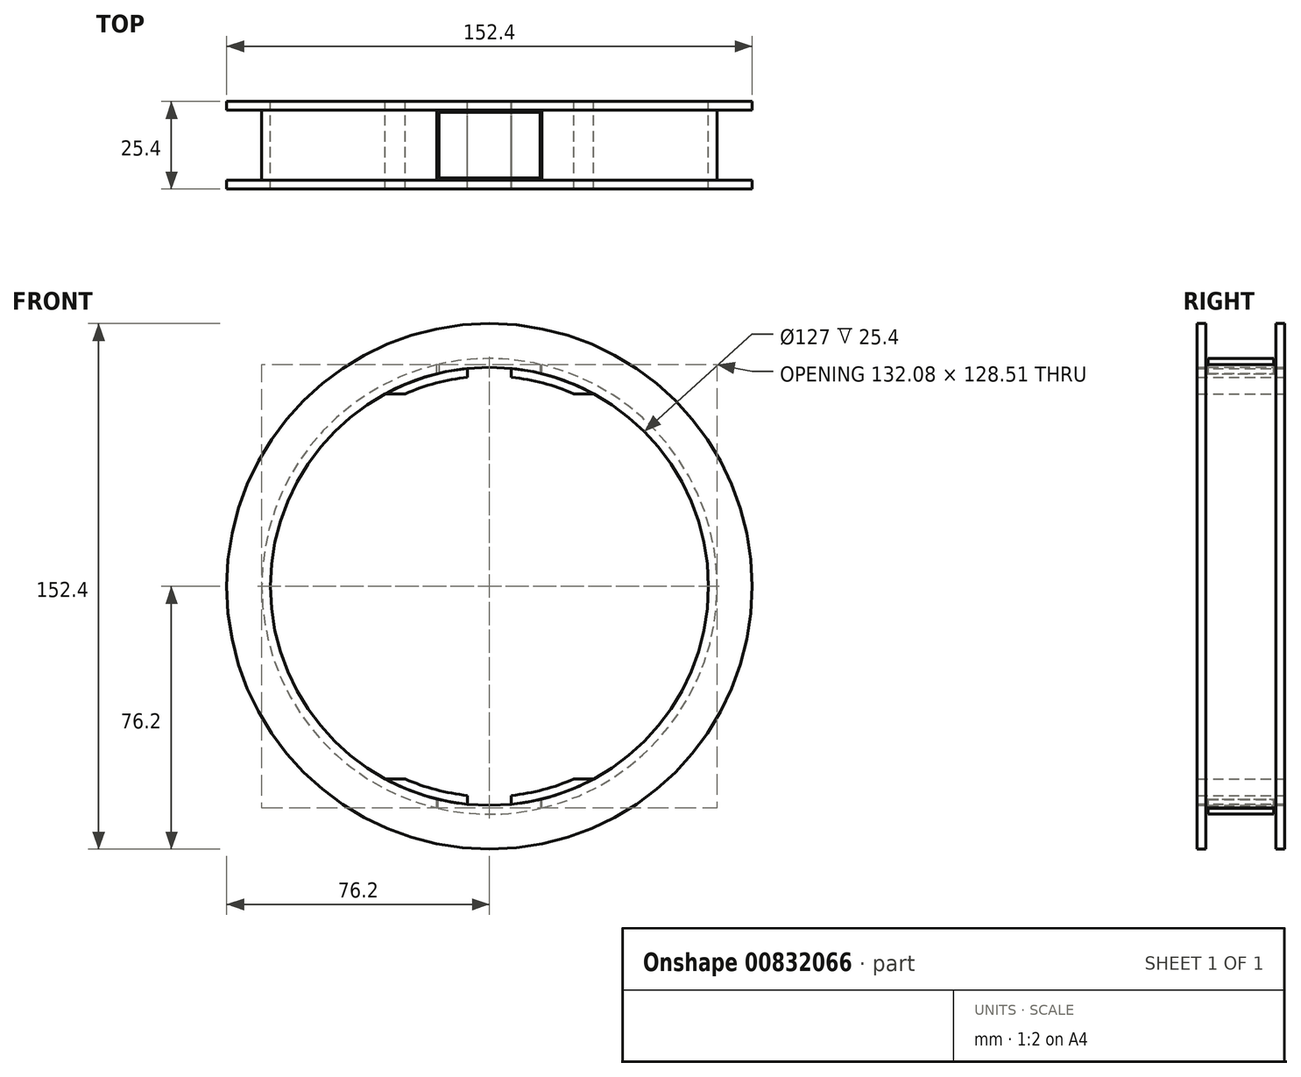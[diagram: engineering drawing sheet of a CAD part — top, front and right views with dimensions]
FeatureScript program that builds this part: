
annotation { "Feature Type Name" : "Feature", "Feature Type Description" : "" }
export const myFeature = defineFeature(function(context is Context, id is Id, definition is map)
    precondition{}
    {
        {
            var Q0;
            Q0=qCreatedBy(makeId("Front.planeOp"),FACE);
            var sketch = newSketch(context, id + "F0", { "sketchPlane" : qUnion([Q0])});
            skCircle(sketch, "E0", {"center": v(0, 0) * mm, "radius": 63.5 * mm});
            skCircle(sketch, "E1", {"center": v(0, 0) * mm, "radius": 76.2 * mm});
            skSolve(sketch);
        }
        {
            var Q0;
            Q0=qSketchRegion(id+"F0",true);
            extrude(context, id + "F1", {"entities" : qUnion([Q0]), "depth" : 25.4 * mm, "offsetDistance" : 25.4 * mm, "symmetric" : true});
        }
        {
            var Q0;
            Q0=qCreatedBy(makeId("Top.planeOp"),FACE);
            var sketch = newSketch(context, id + "F2", { "sketchPlane" : qUnion([Q0])});
            skLineSegment(sketch, "E2", {"start": v(-15.24, -10.16) * mm, "end": v(-15.24, 10.16) * mm});
            skLineSegment(sketch, "E3", {"start": v(15.24, -10.16) * mm, "end": v(15.24, 10.16) * mm});
            skLineSegment(sketch, "E4", {"start": v(15.24, -10.16) * mm, "end": v(-15.24, -10.16) * mm});
            skLineSegment(sketch, "E5", {"start": v(15.24, 10.16) * mm, "end": v(-15.24, 10.16) * mm});
            skLineSegment(sketch, "E6", {"start": v(0, 39.62) * mm, "end": v(0, -54.89) * mm});
            skLineSegment(sketch, "E7", {"start": v(22.27, 0) * mm, "end": v(-22.66, 0) * mm, "construction": true});
            skPoint(sketch, "E7.startSnap0", {"position": v(-15.24, 0) * mm});
            skSolve(sketch);
        }
        {
            var Q0;
            Q0=makeQuery(id+"F1.opExtrude","SWEPT_FACE",FACE,{"disambiguationData":[OSD([sQuery(id+"F0.wireOp",EDGE,"E1")])]});
            shell(context, id + "F3", {"entities" : qUnion([Q0]), "thickness" : 2.54 * mm});
        }
        {
            var Q0;
            Q0=qSketchRegion(id+"F2",true);
            extrude(context, id + "F4", {"entities" : qUnion([Q0]), "operationType" : NewBodyOperationType.REMOVE, "oppositeDirection" : true, "depth" : 132.08 * mm, "offsetDistance" : 25.4 * mm, "symmetric" : true});
        }
        {
            var Q0;
            Q0=qCreatedBy(makeId("Front.planeOp"),FACE);
            var sketch = newSketch(context, id + "F5", { "sketchPlane" : qUnion([Q0])});
            skArc(sketch, "E8", {"start": v(14.74, 61.76) * mm, "mid": v(0.03, 63.5) * mm, "end": v(-14.68, 61.78) * mm});
            skArc(sketch, "E9", {"start": v(-14.96, -64.32) * mm, "mid": v(-0.07, -66.04) * mm, "end": v(14.83, -64.35) * mm});
            skLineSegment(sketch, "E10", {"start": v(-14.68, 64.39) * mm, "end": v(-14.68, 61.78) * mm});
            skLineSegment(sketch, "E11", {"start": v(14.74, 64.37) * mm, "end": v(14.74, 61.76) * mm});
            skLineSegment(sketch, "E12", {"start": v(14.83, -61.74) * mm, "end": v(14.83, -64.35) * mm});
            skLineSegment(sketch, "E13", {"start": v(-14.96, -64.32) * mm, "end": v(-14.96, -61.71) * mm});
            skArc(sketch, "E14.trimOffspring", {"start": v(-14.96, -61.71) * mm, "mid": v(-0.07, -63.5) * mm, "end": v(14.83, -61.74) * mm});
            skArc(sketch, "E15.trimOffspring", {"start": v(14.74, 64.37) * mm, "mid": v(0.03, 66.04) * mm, "end": v(-14.68, 64.39) * mm});
            skSolve(sketch);
        }
        {
            var Q0;
            Q0=qSketchRegion(id+"F5",true);
            extrude(context, id + "F6", {"entities" : qUnion([Q0]), "depth" : 19.05 * mm, "offsetDistance" : 25.4 * mm, "symmetric" : true});
        }
        {
            var Q0;
            Q0=qCreatedBy(makeId("Front.planeOp"),FACE);
            var sketch = newSketch(context, id + "F7", { "sketchPlane" : qUnion([Q0])});
            skArc(sketch, "E16", {"start": v(-24.43, -55.85) * mm, "mid": v(-15.58, -58.94) * mm, "end": v(-6.35, -60.63) * mm});
            skLineSegment(sketch, "E17", {"start": v(-6.35, 60.63) * mm, "end": v(-6.35, 63.17) * mm});
            skLineSegment(sketch, "E18", {"start": v(6.35, 63.17) * mm, "end": v(6.35, 60.63) * mm});
            skLineSegment(sketch, "E19", {"start": v(29.54, 56.4) * mm, "end": v(23.14, 56.4) * mm});
            skLineSegment(sketch, "E20.trimOffspring", {"start": v(-23.14, 56.4) * mm, "end": v(-29.35, 56.4) * mm});
            skLineSegment(sketch, "E21", {"start": v(-6.35, -63.17) * mm, "end": v(-6.35, -60.63) * mm});
            skLineSegment(sketch, "E22", {"start": v(6.35, -63.17) * mm, "end": v(6.35, -60.63) * mm});
            skLineSegment(sketch, "E23", {"start": v(-30.22, -55.85) * mm, "end": v(-24.43, -55.85) * mm});
            skArc(sketch, "E24", {"start": v(-30.22, -55.85) * mm, "mid": v(-18.62, -60.7) * mm, "end": v(-6.29, -63.19) * mm});
            skArc(sketch, "E25.trimOffspring", {"start": v(23.14, 56.4) * mm, "mid": v(14.9, 59.11) * mm, "end": v(6.35, 60.63) * mm});
            skArc(sketch, "E26.trimOffspring", {"start": v(6.35, -60.63) * mm, "mid": v(15.58, -58.94) * mm, "end": v(24.43, -55.85) * mm});
            skArc(sketch, "E27.trimOffspring", {"start": v(-6.35, 60.63) * mm, "mid": v(-14.9, 59.11) * mm, "end": v(-23.14, 56.4) * mm});
            skArc(sketch, "E28.trimOffspring", {"start": v(-6.35, 63.18) * mm, "mid": v(-18.09, 60.87) * mm, "end": v(-29.18, 56.4) * mm});
            skLineSegment(sketch, "E29", {"start": v(24.43, -55.85) * mm, "end": v(30.22, -55.85) * mm});
            skArc(sketch, "E30.trimOffspring", {"start": v(29.18, 56.4) * mm, "mid": v(18.09, 60.87) * mm, "end": v(6.35, 63.18) * mm});
            skArc(sketch, "E31.trimOffspring", {"start": v(6.4, -63.18) * mm, "mid": v(18.67, -60.7) * mm, "end": v(30.22, -55.85) * mm});
            skLineSegment(sketch, "E32.trimOffspring", {"start": v(6.35, -63.13) * mm, "end": v(6.4, -63.18) * mm});
            skLineSegment(sketch, "E33.MirrorCS", {"start": v(-6.35, -63.13) * mm, "end": v(-6.4, -63.18) * mm});
            skArc(sketch, "E34.MirrorCS", {"start": v(-6.35, -60.63) * mm, "mid": v(-15.58, -58.94) * mm, "end": v(-24.43, -55.85) * mm});
            skLineSegment(sketch, "E35.MirrorCS", {"start": v(-24.43, -55.85) * mm, "end": v(-30.22, -55.85) * mm});
            skArc(sketch, "E36.MirrorCS", {"start": v(-6.4, -63.18) * mm, "mid": v(-18.67, -60.7) * mm, "end": v(-30.22, -55.85) * mm});
            skLineSegment(sketch, "E37.MirrorCS", {"start": v(30.22, -55.85) * mm, "end": v(24.43, -55.85) * mm});
            skArc(sketch, "E38.MirrorCS", {"start": v(30.22, -55.85) * mm, "mid": v(18.62, -60.7) * mm, "end": v(6.29, -63.19) * mm});
            skArc(sketch, "E39.MirrorCS", {"start": v(24.43, -55.85) * mm, "mid": v(15.58, -58.94) * mm, "end": v(6.35, -60.63) * mm});
            skLineSegment(sketch, "E40.MirrorCS", {"start": v(6.35, 63.13) * mm, "end": v(6.4, 63.18) * mm});
            skLineSegment(sketch, "E41.MirrorCS", {"start": v(-6.35, 63.13) * mm, "end": v(-6.4, 63.18) * mm});
            skLineSegment(sketch, "E42.MirrorCS", {"start": v(-6.35, 63.17) * mm, "end": v(-6.35, 60.63) * mm});
            skLineSegment(sketch, "E43.MirrorCS", {"start": v(24.43, 55.85) * mm, "end": v(30.22, 55.85) * mm});
            skLineSegment(sketch, "E44.MirrorCS", {"start": v(-24.43, 55.85) * mm, "end": v(-30.22, 55.85) * mm});
            skArc(sketch, "E45.MirrorCS", {"start": v(6.4, 63.18) * mm, "mid": v(18.67, 60.7) * mm, "end": v(30.22, 55.85) * mm});
            skLineSegment(sketch, "E46.MirrorCS", {"start": v(-30.22, 55.85) * mm, "end": v(-24.43, 55.85) * mm});
            skArc(sketch, "E47.MirrorCS", {"start": v(-6.35, 60.63) * mm, "mid": v(-15.58, 58.94) * mm, "end": v(-24.43, 55.85) * mm});
            skArc(sketch, "E48.MirrorCS", {"start": v(-6.4, 63.18) * mm, "mid": v(-18.67, 60.7) * mm, "end": v(-30.22, 55.85) * mm});
            skArc(sketch, "E49.MirrorCS", {"start": v(6.35, 60.63) * mm, "mid": v(15.58, 58.94) * mm, "end": v(24.43, 55.85) * mm});
            skLineSegment(sketch, "E50.MirrorCS", {"start": v(30.22, 55.85) * mm, "end": v(24.43, 55.85) * mm});
            skArc(sketch, "E51.MirrorCS", {"start": v(30.22, 55.85) * mm, "mid": v(18.62, 60.7) * mm, "end": v(6.29, 63.19) * mm});
            skArc(sketch, "E52.MirrorCS", {"start": v(-24.43, 55.85) * mm, "mid": v(-15.58, 58.94) * mm, "end": v(-6.35, 60.63) * mm});
            skArc(sketch, "E53.MirrorCS", {"start": v(24.43, 55.85) * mm, "mid": v(15.58, 58.94) * mm, "end": v(6.35, 60.63) * mm});
            skArc(sketch, "E54.MirrorCS", {"start": v(-30.22, 55.85) * mm, "mid": v(-18.62, 60.7) * mm, "end": v(-6.29, 63.19) * mm});
            skSolve(sketch);
        }
        {
            var Q0;
            Q0=qSketchRegion(id+"F7",true);
            extrude(context, id + "F8", {"entities" : qUnion([Q0]), "depth" : 25.4 * mm, "offsetDistance" : 25.4 * mm, "symmetric" : true});
        }
    });
